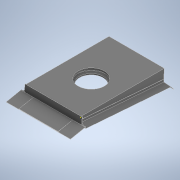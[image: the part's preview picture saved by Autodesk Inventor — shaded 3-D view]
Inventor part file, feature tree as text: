
AUTODESK INVENTOR PART (.ipt)
format: ipt  version: 2022 (Build 260153000, 153)  size: 654,336 bytes
history: native  units: mm
features: sketch x29, extrude x27, chamfer x4, fillet x1, mirror x1
ambient origin geometry x8: Origin, YZ Plane, XZ Plane, XY Plane, X Axis, Y Axis, Z Axis, Center Point
bodies: Solid1 (feature_tree)
feature tree (62):
  extrude  "Extrusion1"  Depth=140.0mm
  extrude  "Extrusion2"  Depth=2.5mm
  extrude  "Extrusion3"  Depth=3.2mm
  extrude  "Extrusion4"  Depth=37.867531mm
  extrude  "Extrusion5"  Depth=1.5mm
  extrude  "Extrusion6"  Depth=2.5mm
  extrude  "Extrusion7"  TaperAngle=0.0deg  [1 undecoded]
  extrude  "Extrusion8"  Depth=100.0mm
  extrude  "Extrusion9"  Depth=1.0mm
  extrude  "Extrusion10"  Depth=16.0mm TaperAngle=0.0deg
  extrude  "Extrusion11"  Depth=1.0mm
  extrude  "Extrusion12"  TaperAngle=0.0deg  [1 undecoded]
  fillet  "Fillet1"  Radius=12.0mm
  chamfer  "Chamfer1"  [1 undecoded]
  extrude  "Extrusion14"  Depth=10.5mm
  extrude  "Extrusion15"  Depth=100.0mm
  sketch  "Sketch23"  dims[d39=27.8mm d40=2.45mm d41=0.0mm d42=0.0mm]
  extrude  "Extrusion16"  TaperAngle=0.0deg  [1 undecoded]
  chamfer  "Chamfer2"  Distance=0.2mm
  extrude  "Extrusion17"  Depth=0.5mm
  extrude  "Extrusion18"  Depth=10.5mm
  extrude  "Extrusion19"  Depth=0.5mm
  extrude  "Extrusion20"  Depth=0.5mm
  extrude  "Extrusion21"  Depth=10.5mm
  sketch  "Sketch32"  dims[d50=105.0deg]
  extrude  "Extrusion22"  Depth=32.0mm TaperAngle=0.0deg
  extrude  "Extrusion23"  Depth=12.0mm TaperAngle=0.0deg
  extrude  "Extrusion24"  Depth=3.0mm TaperAngle=0.0deg
  extrude  "Extrusion25"  Depth=1.5mm
  extrude  "Extrusion26"  Depth=11.0mm TaperAngle=45.0deg
  extrude  "Extrusion27"  Depth=12.0mm TaperAngle=0.0deg
  chamfer  "Chamfer3"  [1 undecoded]
  chamfer  "Chamfer4"  Distance=10.0mm
  extrude  "Extrusion28"  Depth=11.0mm TaperAngle=45.0deg
  mirror  "Mirror1"
  sketch  "Sketch1"  dims[d0=212.0143mm d1=140.0mm]
  sketch  "Sketch2"  dims[d2=2.5mm d3=0.0mm d5=6.45mm]
  sketch  "Sketch3"  dims[d6=40.4609mm d7=0.0mm d8=3.2mm]
  sketch  "Sketch4"  dims[d9=15.009832mm d10=37.867531mm]
  sketch  "Sketch5"  dims[d11=37.96mm d12=1.5mm]
  sketch  "Sketch7"  dims[d14=2.5mm d15=17.453293mm]
  sketch  "Sketch8"  dims[d17=2.5mm d18=0.0mm d19=0.0mm]
  sketch  "Sketch9"  dims[d20=50.0mm d21=100.0mm]
  sketch  "Sketch11"  dims[d23=8.0mm d24=1.0mm]
  sketch  "Sketch12"  dims[d25=17.28mm d26=16.0mm d27=0.0mm]
  sketch  "Sketch13"  dims[d28=1.0mm d30=1.0mm]
  sketch  "Sketch14"  dims[d31=3.0mm d32=0.0mm d33=0.0mm d35=12.0mm d36=0.0mm]
  sketch  "Sketch17"  dims[d37=2.5mm]
  sketch  "Sketch20"  dims[d38=38.3054mm]
  sketch  "Sketch24"  dims[d43=16.406095mm]
  sketch  "Sketch26"  dims[d44=16.89mm]
  sketch  "Sketch27"  dims[d45=17.5mm]
  sketch  "Sketch29"  dims[d46=16.406095mm]
  sketch  "Sketch30"  dims[d47=105.0deg]
  sketch  "Sketch31"  dims[d49=7.15mm]
  sketch  "Sketch33"  dims[d51=6.0mm]
  sketch  "Sketch34"  dims[d52=25.4221mm]
  sketch  "Sketch35"  dims[d56=1.5mm]
  sketch  "Sketch36"  dims[d57=2.3435mm]
  sketch  "Sketch37"  dims[d58=16.231562mm]
  sketch  "Sketch38"  dims[d59=1.5mm]
  sketch  "Sketch39"  dims[d60=9.6051mm d61=0.0mm d62=0.0mm d65=50.0mm d66=100.0mm d67=0.0mm d68=0.0mm d69=0.2mm d70=0.5mm d71=2.55mm d72=0.5mm d73=0.5mm d74=0.8mm d75=32.0mm d76=0.0mm d77=12.0mm d78=0.0mm d79=3.0mm d80=0.0mm d81=1.5mm d85=8.5mm d86=11.0mm d87=45.0deg d88=12.0mm d89=0.0mm d90=0.0mm d91=0.0mm d92=10.0mm d93=0.0mm d94=0.395mm d95=11.0mm d96=45.0deg d97=1.5mm d98=0.8mm d99=6.0mm d100=0.0mm d101=0.5mm d102=2.5mm d103=0.0mm d104=0.0mm d105=40.0mm d106=2.0mm d107=0.0mm d108=0.0mm d109=1.0mm d110=22.2mm d111=0.0mm d112=20.0mm d113=0.0mm d114=86.25mm d115=2.0mm d116=0.0mm d117=16.4392mm d118=0.2mm d119=82.2292mm d121=5.0mm d122=0.0mm d125=67.0mm d126=8.0mm d127=2.5mm d128=0.0mm d129=5.0mm d130=5.0mm d131=0.0mm d132=11.5mm d133=3.0mm d134=0.0mm d135=10.5mm d136=10.5mm d137=0.0mm d138=10.5mm d139=10.5mm d140=45.0deg d141=10.5mm d142=10.5mm d143=45.0deg d144=0.0mm d145=0.0mm]
note: 5 required parameter values undecoded (feature->parameter linkage not recoverable at this tier; creation-order binding heuristic only, values carry confidence <= 0.55)
